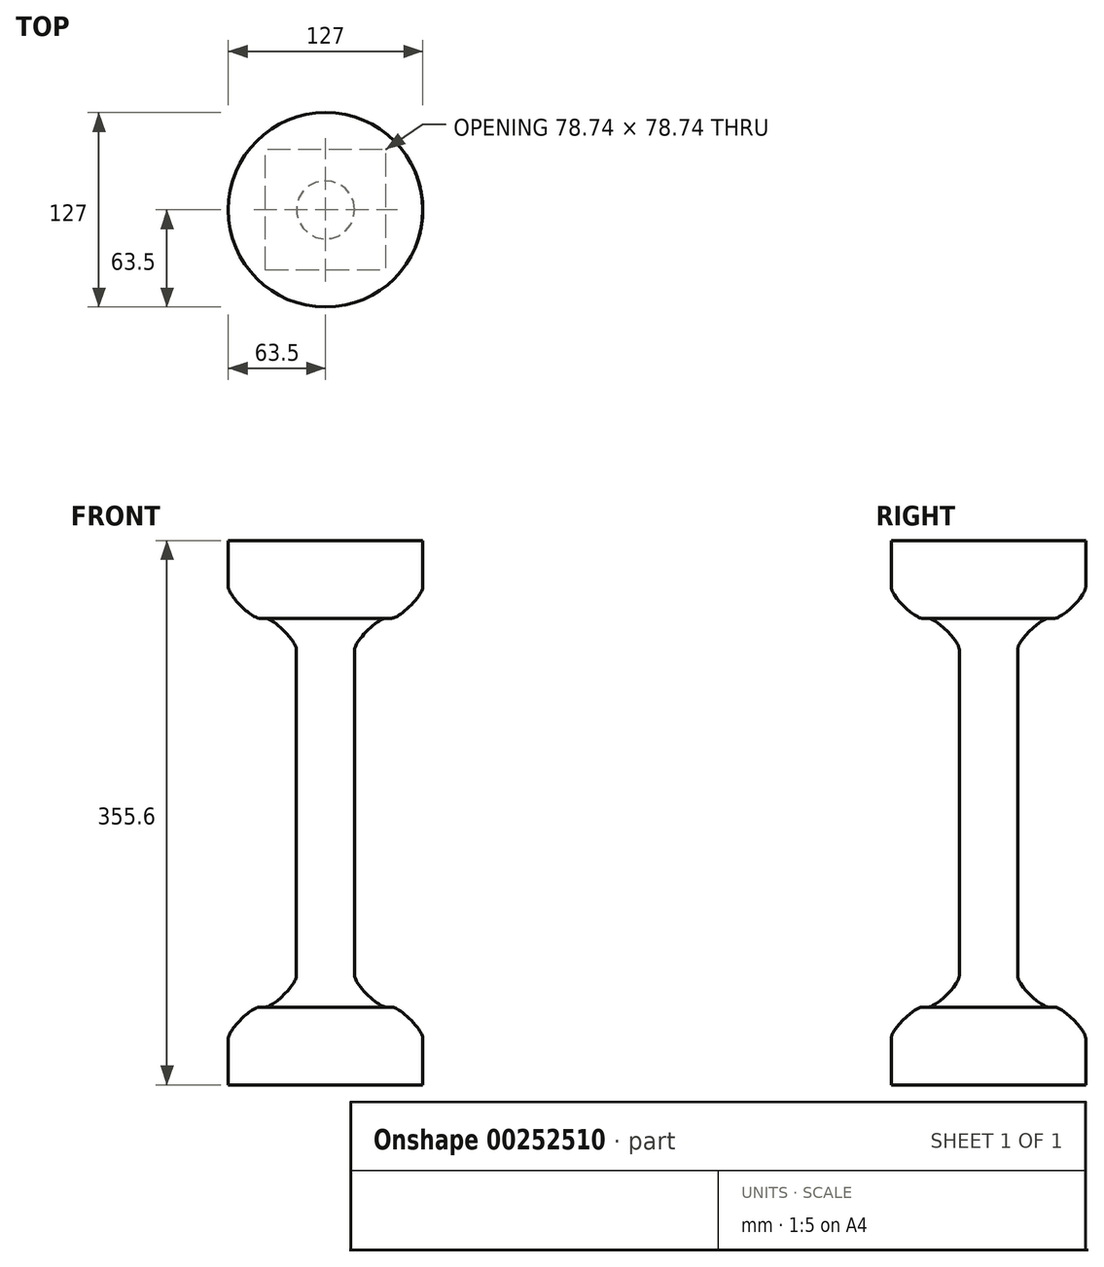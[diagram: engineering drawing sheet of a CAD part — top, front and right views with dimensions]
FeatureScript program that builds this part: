
annotation { "Feature Type Name" : "Feature", "Feature Type Description" : "" }
export const myFeature = defineFeature(function(context is Context, id is Id, definition is map)
    precondition{}
    {
        {
            var Q0;
            Q0=qCreatedBy(makeId("Top.planeOp"),FACE);
            var sketch = newSketch(context, id + "F0", { "sketchPlane" : qUnion([Q0])});
            skCircle(sketch, "E0", {"center": v(0, 0) * mm, "radius": 63.5 * mm});
            skSolve(sketch);
        }
        {
            var Q0;
            Q0=makeQuery(id+"F0.imprint","IMPRINT",FACE,{"disambiguationData":[TD([[makeQuery(id+"F0.imprint","IMPRINT",EDGE,{"derivedFrom":sQuery(id+"F0.wireOp",EDGE,"E0")}),1.0]])]});
            extrude(context, id + "F1", {"entities" : qUnion([Q0]), "depth" : 50.8 * mm});
        }
        {
            var Q0;
            Q0=makeQuery(id+"F1.opExtrude","CAP_FACE",FACE,{"disambiguationData":[OSD([sQuery(id+"F0.wireOp",EDGE,"E0")])],"isStart":false});
            var sketch = newSketch(context, id + "F2", { "sketchPlane" : qUnion([Q0])});
            skCircle(sketch, "E1", {"center": v(0, 0) * mm, "radius": 19.05 * mm});
            skSolve(sketch);
        }
        {
            var Q0;
            Q0=makeQuery(id+"F2.imprint","IMPRINT",FACE,{"disambiguationData":[TD([[makeQuery(id+"F2.imprint","IMPRINT",EDGE,{"derivedFrom":sQuery(id+"F2.wireOp",EDGE,"E1")}),1.0]])]});
            extrude(context, id + "F3", {"entities" : qUnion([Q0]), "operationType" : NewBodyOperationType.ADD, "depth" : 127 * mm});
        }
        {
            var Q0;
            Q0=makeQuery(id+"F1.opExtrude","CAP_FACE",FACE,{"disambiguationData":[OSD([sQuery(id+"F0.wireOp",EDGE,"E0")])],"isStart":false});
            fillet(context, id + "F4", {"entities" : qUnion([Q0]), "radius" : 20.32 * mm, "tangentPropagation" : true, "rho" : .2, "crossSection" : FilletCrossSection.CONIC, "allowEdgeOverflow" : false});
        }
        {
            var Q0;
            Q0=makeQuery(id+"F1.opExtrude","SWEPT_BODY",BODY,{"disambiguationData":[OSD([sQuery(id+"F0.wireOp",EDGE,"E0")])]});
            var Q1;
            Q1=makeQuery(id+"F3.opExtrude","CAP_FACE",FACE,{"disambiguationData":[OSD([sQuery(id+"F2.wireOp",EDGE,"E1")])],"isStart":false});
            mirror(context, id + "F5", {"operationType" : NewBodyOperationType.ADD, "entities" : qUnion([Q0]), "mirrorPlane" : qUnion([Q1])});
        }
    });
